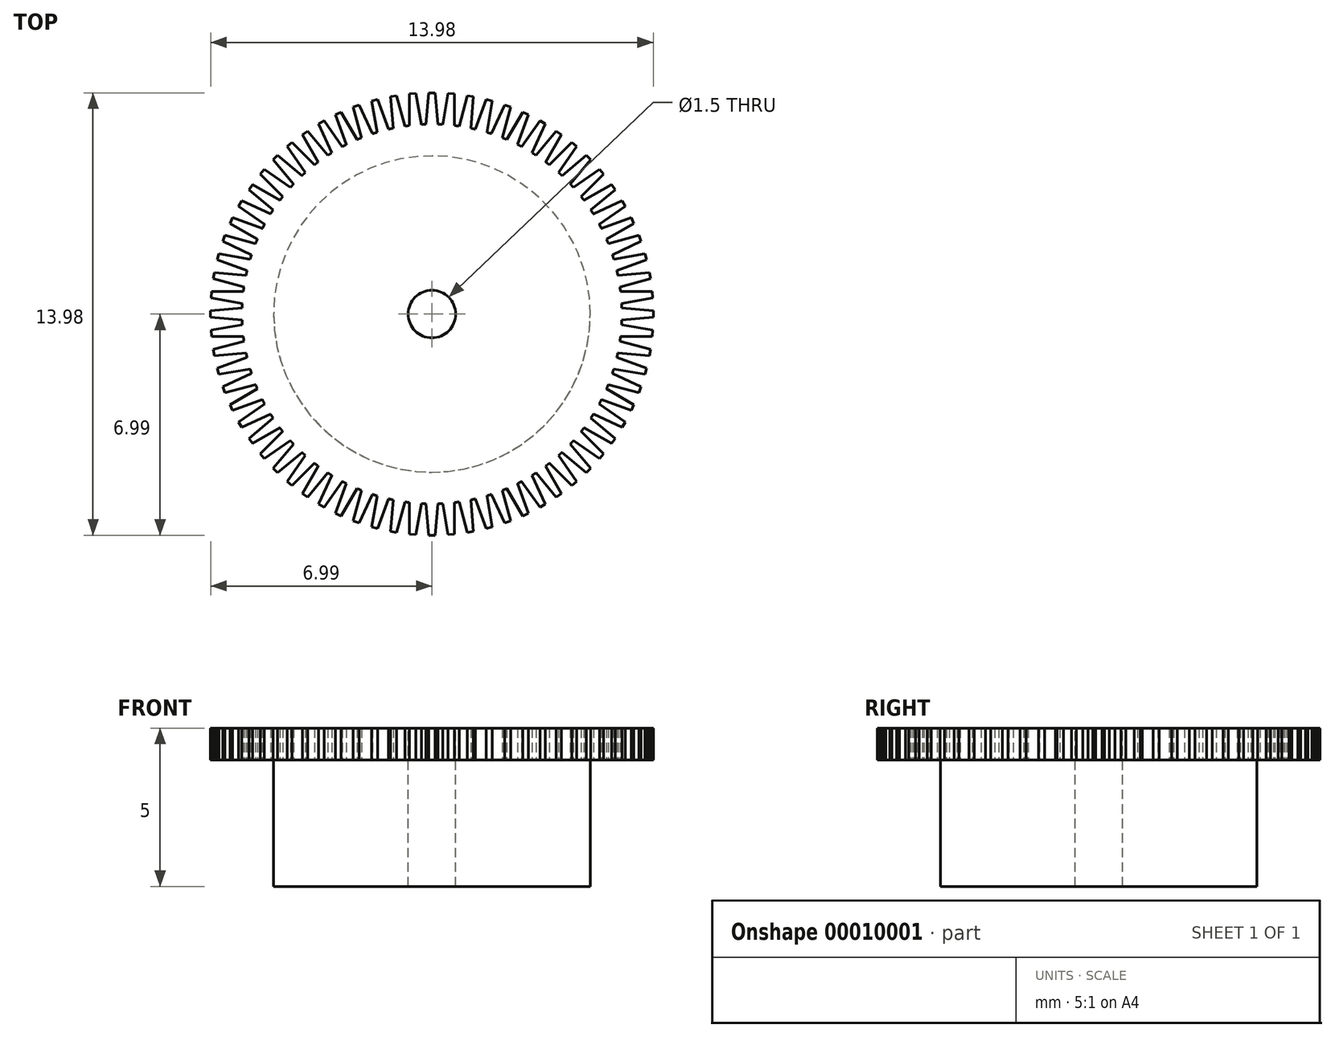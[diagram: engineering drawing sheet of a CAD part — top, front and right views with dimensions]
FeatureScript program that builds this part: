
annotation { "Feature Type Name" : "Feature", "Feature Type Description" : "" }
export const myFeature = defineFeature(function(context is Context, id is Id, definition is map)
    precondition{}
    {
        {
            var Q0;
            Q0=qCreatedBy(makeId("Top.planeOp"),FACE);
            var sketch = newSketch(context, id + "F0", { "sketchPlane" : qUnion([Q0])});
            skCircle(sketch, "E0", {"center": v(0, 0) * mm, "radius": 6 * mm});
            skLineSegment(sketch, "E1", {"start": v(0, 0) * mm, "end": v(0, 6) * mm, "construction": true});
            skLineSegment(sketch, "E2", {"start": v(-0.19, 6) * mm, "end": v(-0.1, 7) * mm});
            skLineSegment(sketch, "E3", {"start": v(-0.1, 7) * mm, "end": v(0, 7) * mm});
            skLineSegment(sketch, "E4.0.MirrorCS", {"start": v(0.1, 7) * mm, "end": v(0, 7) * mm});
            skLineSegment(sketch, "E5.0.MirrorCS", {"start": v(0.19, 6) * mm, "end": v(0.1, 7) * mm});
            skLineSegment(sketch, "E6.1.0", {"start": v(-0.7, 5.96) * mm, "end": v(-0.7, 6.96) * mm});
            skLineSegment(sketch, "E6.1.1", {"start": v(-0.7, 6.96) * mm, "end": v(-0.6, 6.97) * mm});
            skLineSegment(sketch, "E6.1.2", {"start": v(-0.5, 6.98) * mm, "end": v(-0.6, 6.97) * mm});
            skLineSegment(sketch, "E6.1.3", {"start": v(-0.34, 6) * mm, "end": v(-0.5, 6.98) * mm});
            skLineSegment(sketch, "E6.2.0", {"start": v(-1.23, 5.87) * mm, "end": v(-1.31, 6.87) * mm});
            skLineSegment(sketch, "E6.2.1", {"start": v(-1.31, 6.87) * mm, "end": v(-1.21, 6.89) * mm});
            skLineSegment(sketch, "E6.2.2", {"start": v(-1.12, 6.9) * mm, "end": v(-1.21, 6.89) * mm});
            skLineSegment(sketch, "E6.2.3", {"start": v(-0.86, 5.94) * mm, "end": v(-1.12, 6.9) * mm});
            skLineSegment(sketch, "E6.3.0", {"start": v(-1.73, 5.74) * mm, "end": v(-1.9, 6.73) * mm});
            skLineSegment(sketch, "E6.3.1", {"start": v(-1.9, 6.73) * mm, "end": v(-1.8, 6.75) * mm});
            skLineSegment(sketch, "E6.3.2", {"start": v(-1.71, 6.78) * mm, "end": v(-1.8, 6.75) * mm});
            skLineSegment(sketch, "E6.3.3", {"start": v(-1.37, 5.84) * mm, "end": v(-1.71, 6.78) * mm});
            skLineSegment(sketch, "E6.4.0", {"start": v(-2.23, 5.57) * mm, "end": v(-2.49, 6.54) * mm});
            skLineSegment(sketch, "E6.4.1", {"start": v(-2.49, 6.54) * mm, "end": v(-2.4, 6.57) * mm});
            skLineSegment(sketch, "E6.4.2", {"start": v(-2.3, 6.6) * mm, "end": v(-2.4, 6.57) * mm});
            skLineSegment(sketch, "E6.4.3", {"start": v(-1.88, 5.7) * mm, "end": v(-2.3, 6.6) * mm});
            skLineSegment(sketch, "E6.5.0", {"start": v(-2.7, 5.36) * mm, "end": v(-3.05, 6.3) * mm});
            skLineSegment(sketch, "E6.5.1", {"start": v(-3.05, 6.3) * mm, "end": v(-2.96, 6.34) * mm});
            skLineSegment(sketch, "E6.5.2", {"start": v(-2.86, 6.38) * mm, "end": v(-2.96, 6.34) * mm});
            skLineSegment(sketch, "E6.5.3", {"start": v(-2.36, 5.51) * mm, "end": v(-2.86, 6.38) * mm});
            skLineSegment(sketch, "E6.6.0", {"start": v(-3.16, 5.1) * mm, "end": v(-3.58, 6) * mm});
            skLineSegment(sketch, "E6.6.1", {"start": v(-3.58, 6) * mm, "end": v(-3.5, 6.06) * mm});
            skLineSegment(sketch, "E6.6.2", {"start": v(-3.41, 6.1) * mm, "end": v(-3.5, 6.06) * mm});
            skLineSegment(sketch, "E6.6.3", {"start": v(-2.84, 5.29) * mm, "end": v(-3.41, 6.1) * mm});
            skLineSegment(sketch, "E6.7.0", {"start": v(-3.6, 4.8) * mm, "end": v(-4.1, 5.67) * mm});
            skLineSegment(sketch, "E6.7.1", {"start": v(-4.1, 5.67) * mm, "end": v(-4.01, 5.73) * mm});
            skLineSegment(sketch, "E6.7.2", {"start": v(-3.93, 5.79) * mm, "end": v(-4.01, 5.73) * mm});
            skLineSegment(sketch, "E6.7.3", {"start": v(-3.29, 5.02) * mm, "end": v(-3.93, 5.79) * mm});
            skLineSegment(sketch, "E6.8.0", {"start": v(-4, 4.47) * mm, "end": v(-4.57, 5.3) * mm});
            skLineSegment(sketch, "E6.8.1", {"start": v(-4.57, 5.3) * mm, "end": v(-4.5, 5.36) * mm});
            skLineSegment(sketch, "E6.8.2", {"start": v(-4.42, 5.42) * mm, "end": v(-4.5, 5.36) * mm});
            skLineSegment(sketch, "E6.8.3", {"start": v(-3.71, 4.71) * mm, "end": v(-4.42, 5.42) * mm});
            skLineSegment(sketch, "E6.9.0", {"start": v(-4.37, 4.1) * mm, "end": v(-5.02, 4.87) * mm});
            skLineSegment(sketch, "E6.9.1", {"start": v(-5.02, 4.87) * mm, "end": v(-4.94, 4.94) * mm});
            skLineSegment(sketch, "E6.9.2", {"start": v(-4.87, 5.02) * mm, "end": v(-4.94, 4.94) * mm});
            skLineSegment(sketch, "E6.9.3", {"start": v(-4.1, 4.37) * mm, "end": v(-4.87, 5.02) * mm});
            skLineSegment(sketch, "E6.10.0", {"start": v(-4.71, 3.71) * mm, "end": v(-5.42, 4.42) * mm});
            skLineSegment(sketch, "E6.10.1", {"start": v(-5.42, 4.42) * mm, "end": v(-5.36, 4.5) * mm});
            skLineSegment(sketch, "E6.10.2", {"start": v(-5.3, 4.57) * mm, "end": v(-5.36, 4.5) * mm});
            skLineSegment(sketch, "E6.10.3", {"start": v(-4.47, 4) * mm, "end": v(-5.3, 4.57) * mm});
            skLineSegment(sketch, "E6.11.0", {"start": v(-5.02, 3.29) * mm, "end": v(-5.79, 3.93) * mm});
            skLineSegment(sketch, "E6.11.1", {"start": v(-5.79, 3.93) * mm, "end": v(-5.73, 4.01) * mm});
            skLineSegment(sketch, "E6.11.2", {"start": v(-5.67, 4.1) * mm, "end": v(-5.73, 4.01) * mm});
            skLineSegment(sketch, "E6.11.3", {"start": v(-4.8, 3.6) * mm, "end": v(-5.67, 4.1) * mm});
            skLineSegment(sketch, "E6.12.0", {"start": v(-5.29, 2.84) * mm, "end": v(-6.1, 3.41) * mm});
            skLineSegment(sketch, "E6.12.1", {"start": v(-6.1, 3.41) * mm, "end": v(-6.06, 3.5) * mm});
            skLineSegment(sketch, "E6.12.2", {"start": v(-6, 3.58) * mm, "end": v(-6.06, 3.5) * mm});
            skLineSegment(sketch, "E6.12.3", {"start": v(-5.1, 3.16) * mm, "end": v(-6, 3.58) * mm});
            skLineSegment(sketch, "E6.13.0", {"start": v(-5.51, 2.36) * mm, "end": v(-6.38, 2.86) * mm});
            skLineSegment(sketch, "E6.13.1", {"start": v(-6.38, 2.86) * mm, "end": v(-6.34, 2.96) * mm});
            skLineSegment(sketch, "E6.13.2", {"start": v(-6.3, 3.05) * mm, "end": v(-6.34, 2.96) * mm});
            skLineSegment(sketch, "E6.13.3", {"start": v(-5.36, 2.7) * mm, "end": v(-6.3, 3.05) * mm});
            skLineSegment(sketch, "E6.14.0", {"start": v(-5.7, 1.88) * mm, "end": v(-6.6, 2.3) * mm});
            skLineSegment(sketch, "E6.14.1", {"start": v(-6.6, 2.3) * mm, "end": v(-6.57, 2.4) * mm});
            skLineSegment(sketch, "E6.14.2", {"start": v(-6.54, 2.49) * mm, "end": v(-6.57, 2.4) * mm});
            skLineSegment(sketch, "E6.14.3", {"start": v(-5.57, 2.23) * mm, "end": v(-6.54, 2.49) * mm});
            skLineSegment(sketch, "E6.15.0", {"start": v(-5.84, 1.37) * mm, "end": v(-6.78, 1.71) * mm});
            skLineSegment(sketch, "E6.15.1", {"start": v(-6.78, 1.71) * mm, "end": v(-6.75, 1.8) * mm});
            skLineSegment(sketch, "E6.15.2", {"start": v(-6.73, 1.9) * mm, "end": v(-6.75, 1.8) * mm});
            skLineSegment(sketch, "E6.15.3", {"start": v(-5.74, 1.73) * mm, "end": v(-6.73, 1.9) * mm});
            skLineSegment(sketch, "E6.16.0", {"start": v(-5.94, 0.86) * mm, "end": v(-6.9, 1.12) * mm});
            skLineSegment(sketch, "E6.16.1", {"start": v(-6.9, 1.12) * mm, "end": v(-6.89, 1.21) * mm});
            skLineSegment(sketch, "E6.16.2", {"start": v(-6.87, 1.31) * mm, "end": v(-6.89, 1.21) * mm});
            skLineSegment(sketch, "E6.16.3", {"start": v(-5.87, 1.23) * mm, "end": v(-6.87, 1.31) * mm});
            skLineSegment(sketch, "E6.17.0", {"start": v(-6, 0.34) * mm, "end": v(-6.98, 0.5) * mm});
            skLineSegment(sketch, "E6.17.1", {"start": v(-6.98, 0.5) * mm, "end": v(-6.97, 0.6) * mm});
            skLineSegment(sketch, "E6.17.2", {"start": v(-6.96, 0.7) * mm, "end": v(-6.97, 0.6) * mm});
            skLineSegment(sketch, "E6.17.3", {"start": v(-5.96, 0.7) * mm, "end": v(-6.96, 0.7) * mm});
            skLineSegment(sketch, "E6.18.0", {"start": v(-6, -0.19) * mm, "end": v(-7, -0.1) * mm});
            skLineSegment(sketch, "E6.18.1", {"start": v(-7, -0.1) * mm, "end": v(-7, 0) * mm});
            skLineSegment(sketch, "E6.18.2", {"start": v(-7, 0.1) * mm, "end": v(-7, 0) * mm});
            skLineSegment(sketch, "E6.18.3", {"start": v(-6, 0.19) * mm, "end": v(-7, 0.1) * mm});
            skLineSegment(sketch, "E6.19.0", {"start": v(-5.96, -0.7) * mm, "end": v(-6.96, -0.7) * mm});
            skLineSegment(sketch, "E6.19.1", {"start": v(-6.96, -0.7) * mm, "end": v(-6.97, -0.6) * mm});
            skLineSegment(sketch, "E6.19.2", {"start": v(-6.98, -0.5) * mm, "end": v(-6.97, -0.6) * mm});
            skLineSegment(sketch, "E6.19.3", {"start": v(-6, -0.34) * mm, "end": v(-6.98, -0.5) * mm});
            skLineSegment(sketch, "E6.20.0", {"start": v(-5.87, -1.23) * mm, "end": v(-6.87, -1.31) * mm});
            skLineSegment(sketch, "E6.20.1", {"start": v(-6.87, -1.31) * mm, "end": v(-6.89, -1.21) * mm});
            skLineSegment(sketch, "E6.20.2", {"start": v(-6.9, -1.12) * mm, "end": v(-6.89, -1.21) * mm});
            skLineSegment(sketch, "E6.20.3", {"start": v(-5.94, -0.86) * mm, "end": v(-6.9, -1.12) * mm});
            skLineSegment(sketch, "E6.21.0", {"start": v(-5.74, -1.73) * mm, "end": v(-6.73, -1.9) * mm});
            skLineSegment(sketch, "E6.21.1", {"start": v(-6.73, -1.9) * mm, "end": v(-6.75, -1.8) * mm});
            skLineSegment(sketch, "E6.21.2", {"start": v(-6.78, -1.71) * mm, "end": v(-6.75, -1.8) * mm});
            skLineSegment(sketch, "E6.21.3", {"start": v(-5.84, -1.37) * mm, "end": v(-6.78, -1.71) * mm});
            skLineSegment(sketch, "E6.22.0", {"start": v(-5.57, -2.23) * mm, "end": v(-6.54, -2.49) * mm});
            skLineSegment(sketch, "E6.22.1", {"start": v(-6.54, -2.49) * mm, "end": v(-6.57, -2.4) * mm});
            skLineSegment(sketch, "E6.22.2", {"start": v(-6.6, -2.3) * mm, "end": v(-6.57, -2.4) * mm});
            skLineSegment(sketch, "E6.22.3", {"start": v(-5.7, -1.88) * mm, "end": v(-6.6, -2.3) * mm});
            skLineSegment(sketch, "E6.23.0", {"start": v(-5.36, -2.7) * mm, "end": v(-6.3, -3.05) * mm});
            skLineSegment(sketch, "E6.23.1", {"start": v(-6.3, -3.05) * mm, "end": v(-6.34, -2.96) * mm});
            skLineSegment(sketch, "E6.23.2", {"start": v(-6.38, -2.86) * mm, "end": v(-6.34, -2.96) * mm});
            skLineSegment(sketch, "E6.23.3", {"start": v(-5.51, -2.36) * mm, "end": v(-6.38, -2.86) * mm});
            skLineSegment(sketch, "E6.24.0", {"start": v(-5.1, -3.16) * mm, "end": v(-6, -3.58) * mm});
            skLineSegment(sketch, "E6.24.1", {"start": v(-6, -3.58) * mm, "end": v(-6.06, -3.5) * mm});
            skLineSegment(sketch, "E6.24.2", {"start": v(-6.1, -3.41) * mm, "end": v(-6.06, -3.5) * mm});
            skLineSegment(sketch, "E6.24.3", {"start": v(-5.29, -2.84) * mm, "end": v(-6.1, -3.41) * mm});
            skLineSegment(sketch, "E6.25.0", {"start": v(-4.8, -3.6) * mm, "end": v(-5.67, -4.1) * mm});
            skLineSegment(sketch, "E6.25.1", {"start": v(-5.67, -4.1) * mm, "end": v(-5.73, -4.01) * mm});
            skLineSegment(sketch, "E6.25.2", {"start": v(-5.79, -3.93) * mm, "end": v(-5.73, -4.01) * mm});
            skLineSegment(sketch, "E6.25.3", {"start": v(-5.02, -3.29) * mm, "end": v(-5.79, -3.93) * mm});
            skLineSegment(sketch, "E6.26.0", {"start": v(-4.47, -4) * mm, "end": v(-5.3, -4.57) * mm});
            skLineSegment(sketch, "E6.26.1", {"start": v(-5.3, -4.57) * mm, "end": v(-5.36, -4.5) * mm});
            skLineSegment(sketch, "E6.26.2", {"start": v(-5.42, -4.42) * mm, "end": v(-5.36, -4.5) * mm});
            skLineSegment(sketch, "E6.26.3", {"start": v(-4.71, -3.71) * mm, "end": v(-5.42, -4.42) * mm});
            skLineSegment(sketch, "E6.27.0", {"start": v(-4.1, -4.37) * mm, "end": v(-4.87, -5.02) * mm});
            skLineSegment(sketch, "E6.27.1", {"start": v(-4.87, -5.02) * mm, "end": v(-4.94, -4.94) * mm});
            skLineSegment(sketch, "E6.27.2", {"start": v(-5.02, -4.87) * mm, "end": v(-4.94, -4.94) * mm});
            skLineSegment(sketch, "E6.27.3", {"start": v(-4.37, -4.1) * mm, "end": v(-5.02, -4.87) * mm});
            skLineSegment(sketch, "E6.28.0", {"start": v(-3.71, -4.71) * mm, "end": v(-4.42, -5.42) * mm});
            skLineSegment(sketch, "E6.28.1", {"start": v(-4.42, -5.42) * mm, "end": v(-4.5, -5.36) * mm});
            skLineSegment(sketch, "E6.28.2", {"start": v(-4.57, -5.3) * mm, "end": v(-4.5, -5.36) * mm});
            skLineSegment(sketch, "E6.28.3", {"start": v(-4, -4.47) * mm, "end": v(-4.57, -5.3) * mm});
            skLineSegment(sketch, "E6.29.0", {"start": v(-3.29, -5.02) * mm, "end": v(-3.93, -5.79) * mm});
            skLineSegment(sketch, "E6.29.1", {"start": v(-3.93, -5.79) * mm, "end": v(-4.01, -5.73) * mm});
            skLineSegment(sketch, "E6.29.2", {"start": v(-4.1, -5.67) * mm, "end": v(-4.01, -5.73) * mm});
            skLineSegment(sketch, "E6.29.3", {"start": v(-3.6, -4.8) * mm, "end": v(-4.1, -5.67) * mm});
            skLineSegment(sketch, "E6.30.0", {"start": v(-2.84, -5.29) * mm, "end": v(-3.41, -6.1) * mm});
            skLineSegment(sketch, "E6.30.1", {"start": v(-3.41, -6.1) * mm, "end": v(-3.5, -6.06) * mm});
            skLineSegment(sketch, "E6.30.2", {"start": v(-3.58, -6) * mm, "end": v(-3.5, -6.06) * mm});
            skLineSegment(sketch, "E6.30.3", {"start": v(-3.16, -5.1) * mm, "end": v(-3.58, -6) * mm});
            skLineSegment(sketch, "E6.31.0", {"start": v(-2.36, -5.51) * mm, "end": v(-2.86, -6.38) * mm});
            skLineSegment(sketch, "E6.31.1", {"start": v(-2.86, -6.38) * mm, "end": v(-2.96, -6.34) * mm});
            skLineSegment(sketch, "E6.31.2", {"start": v(-3.05, -6.3) * mm, "end": v(-2.96, -6.34) * mm});
            skLineSegment(sketch, "E6.31.3", {"start": v(-2.7, -5.36) * mm, "end": v(-3.05, -6.3) * mm});
            skLineSegment(sketch, "E6.32.0", {"start": v(-1.88, -5.7) * mm, "end": v(-2.3, -6.6) * mm});
            skLineSegment(sketch, "E6.32.1", {"start": v(-2.3, -6.6) * mm, "end": v(-2.4, -6.57) * mm});
            skLineSegment(sketch, "E6.32.2", {"start": v(-2.49, -6.54) * mm, "end": v(-2.4, -6.57) * mm});
            skLineSegment(sketch, "E6.32.3", {"start": v(-2.23, -5.57) * mm, "end": v(-2.49, -6.54) * mm});
            skLineSegment(sketch, "E6.33.0", {"start": v(-1.37, -5.84) * mm, "end": v(-1.71, -6.78) * mm});
            skLineSegment(sketch, "E6.33.1", {"start": v(-1.71, -6.78) * mm, "end": v(-1.8, -6.75) * mm});
            skLineSegment(sketch, "E6.33.2", {"start": v(-1.9, -6.73) * mm, "end": v(-1.8, -6.75) * mm});
            skLineSegment(sketch, "E6.33.3", {"start": v(-1.73, -5.74) * mm, "end": v(-1.9, -6.73) * mm});
            skLineSegment(sketch, "E6.34.0", {"start": v(-0.86, -5.94) * mm, "end": v(-1.12, -6.9) * mm});
            skLineSegment(sketch, "E6.34.1", {"start": v(-1.12, -6.9) * mm, "end": v(-1.21, -6.89) * mm});
            skLineSegment(sketch, "E6.34.2", {"start": v(-1.31, -6.87) * mm, "end": v(-1.21, -6.89) * mm});
            skLineSegment(sketch, "E6.34.3", {"start": v(-1.23, -5.87) * mm, "end": v(-1.31, -6.87) * mm});
            skLineSegment(sketch, "E6.35.0", {"start": v(-0.34, -6) * mm, "end": v(-0.5, -6.98) * mm});
            skLineSegment(sketch, "E6.35.1", {"start": v(-0.5, -6.98) * mm, "end": v(-0.6, -6.97) * mm});
            skLineSegment(sketch, "E6.35.2", {"start": v(-0.7, -6.96) * mm, "end": v(-0.6, -6.97) * mm});
            skLineSegment(sketch, "E6.35.3", {"start": v(-0.7, -5.96) * mm, "end": v(-0.7, -6.96) * mm});
            skLineSegment(sketch, "E6.36.0", {"start": v(0.19, -6) * mm, "end": v(0.1, -7) * mm});
            skLineSegment(sketch, "E6.36.1", {"start": v(0.1, -7) * mm, "end": v(0, -7) * mm});
            skLineSegment(sketch, "E6.36.2", {"start": v(-0.1, -7) * mm, "end": v(0, -7) * mm});
            skLineSegment(sketch, "E6.36.3", {"start": v(-0.19, -6) * mm, "end": v(-0.1, -7) * mm});
            skLineSegment(sketch, "E6.37.0", {"start": v(0.7, -5.96) * mm, "end": v(0.7, -6.96) * mm});
            skLineSegment(sketch, "E6.37.1", {"start": v(0.7, -6.96) * mm, "end": v(0.6, -6.97) * mm});
            skLineSegment(sketch, "E6.37.2", {"start": v(0.5, -6.98) * mm, "end": v(0.6, -6.97) * mm});
            skLineSegment(sketch, "E6.37.3", {"start": v(0.34, -6) * mm, "end": v(0.5, -6.98) * mm});
            skLineSegment(sketch, "E6.38.0", {"start": v(1.23, -5.87) * mm, "end": v(1.31, -6.87) * mm});
            skLineSegment(sketch, "E6.38.1", {"start": v(1.31, -6.87) * mm, "end": v(1.21, -6.89) * mm});
            skLineSegment(sketch, "E6.38.2", {"start": v(1.12, -6.9) * mm, "end": v(1.21, -6.89) * mm});
            skLineSegment(sketch, "E6.38.3", {"start": v(0.86, -5.94) * mm, "end": v(1.12, -6.9) * mm});
            skLineSegment(sketch, "E6.39.0", {"start": v(1.73, -5.74) * mm, "end": v(1.9, -6.73) * mm});
            skLineSegment(sketch, "E6.39.1", {"start": v(1.9, -6.73) * mm, "end": v(1.8, -6.75) * mm});
            skLineSegment(sketch, "E6.39.2", {"start": v(1.71, -6.78) * mm, "end": v(1.8, -6.75) * mm});
            skLineSegment(sketch, "E6.39.3", {"start": v(1.37, -5.84) * mm, "end": v(1.71, -6.78) * mm});
            skLineSegment(sketch, "E6.40.0", {"start": v(2.23, -5.57) * mm, "end": v(2.49, -6.54) * mm});
            skLineSegment(sketch, "E6.40.1", {"start": v(2.49, -6.54) * mm, "end": v(2.4, -6.57) * mm});
            skLineSegment(sketch, "E6.40.2", {"start": v(2.3, -6.6) * mm, "end": v(2.4, -6.57) * mm});
            skLineSegment(sketch, "E6.40.3", {"start": v(1.88, -5.7) * mm, "end": v(2.3, -6.6) * mm});
            skLineSegment(sketch, "E6.41.0", {"start": v(2.7, -5.36) * mm, "end": v(3.05, -6.3) * mm});
            skLineSegment(sketch, "E6.41.1", {"start": v(3.05, -6.3) * mm, "end": v(2.96, -6.34) * mm});
            skLineSegment(sketch, "E6.41.2", {"start": v(2.86, -6.38) * mm, "end": v(2.96, -6.34) * mm});
            skLineSegment(sketch, "E6.41.3", {"start": v(2.36, -5.51) * mm, "end": v(2.86, -6.38) * mm});
            skLineSegment(sketch, "E6.42.0", {"start": v(3.16, -5.1) * mm, "end": v(3.58, -6) * mm});
            skLineSegment(sketch, "E6.42.1", {"start": v(3.58, -6) * mm, "end": v(3.5, -6.06) * mm});
            skLineSegment(sketch, "E6.42.2", {"start": v(3.41, -6.1) * mm, "end": v(3.5, -6.06) * mm});
            skLineSegment(sketch, "E6.42.3", {"start": v(2.84, -5.29) * mm, "end": v(3.41, -6.1) * mm});
            skLineSegment(sketch, "E6.43.0", {"start": v(3.6, -4.8) * mm, "end": v(4.1, -5.67) * mm});
            skLineSegment(sketch, "E6.43.1", {"start": v(4.1, -5.67) * mm, "end": v(4.01, -5.73) * mm});
            skLineSegment(sketch, "E6.43.2", {"start": v(3.93, -5.79) * mm, "end": v(4.01, -5.73) * mm});
            skLineSegment(sketch, "E6.43.3", {"start": v(3.29, -5.02) * mm, "end": v(3.93, -5.79) * mm});
            skLineSegment(sketch, "E6.44.0", {"start": v(4, -4.47) * mm, "end": v(4.57, -5.3) * mm});
            skLineSegment(sketch, "E6.44.1", {"start": v(4.57, -5.3) * mm, "end": v(4.5, -5.36) * mm});
            skLineSegment(sketch, "E6.44.2", {"start": v(4.42, -5.42) * mm, "end": v(4.5, -5.36) * mm});
            skLineSegment(sketch, "E6.44.3", {"start": v(3.71, -4.71) * mm, "end": v(4.42, -5.42) * mm});
            skLineSegment(sketch, "E6.45.0", {"start": v(4.37, -4.1) * mm, "end": v(5.02, -4.87) * mm});
            skLineSegment(sketch, "E6.45.1", {"start": v(5.02, -4.87) * mm, "end": v(4.94, -4.94) * mm});
            skLineSegment(sketch, "E6.45.2", {"start": v(4.87, -5.02) * mm, "end": v(4.94, -4.94) * mm});
            skLineSegment(sketch, "E6.45.3", {"start": v(4.1, -4.37) * mm, "end": v(4.87, -5.02) * mm});
            skLineSegment(sketch, "E6.46.0", {"start": v(4.71, -3.71) * mm, "end": v(5.42, -4.42) * mm});
            skLineSegment(sketch, "E6.46.1", {"start": v(5.42, -4.42) * mm, "end": v(5.36, -4.5) * mm});
            skLineSegment(sketch, "E6.46.2", {"start": v(5.3, -4.57) * mm, "end": v(5.36, -4.5) * mm});
            skLineSegment(sketch, "E6.46.3", {"start": v(4.47, -4) * mm, "end": v(5.3, -4.57) * mm});
            skLineSegment(sketch, "E6.47.0", {"start": v(5.02, -3.29) * mm, "end": v(5.79, -3.93) * mm});
            skLineSegment(sketch, "E6.47.1", {"start": v(5.79, -3.93) * mm, "end": v(5.73, -4.01) * mm});
            skLineSegment(sketch, "E6.47.2", {"start": v(5.67, -4.1) * mm, "end": v(5.73, -4.01) * mm});
            skLineSegment(sketch, "E6.47.3", {"start": v(4.8, -3.6) * mm, "end": v(5.67, -4.1) * mm});
            skLineSegment(sketch, "E6.48.0", {"start": v(5.29, -2.84) * mm, "end": v(6.1, -3.41) * mm});
            skLineSegment(sketch, "E6.48.1", {"start": v(6.1, -3.41) * mm, "end": v(6.06, -3.5) * mm});
            skLineSegment(sketch, "E6.48.2", {"start": v(6, -3.58) * mm, "end": v(6.06, -3.5) * mm});
            skLineSegment(sketch, "E6.48.3", {"start": v(5.1, -3.16) * mm, "end": v(6, -3.58) * mm});
            skLineSegment(sketch, "E6.49.0", {"start": v(5.51, -2.36) * mm, "end": v(6.38, -2.86) * mm});
            skLineSegment(sketch, "E6.49.1", {"start": v(6.38, -2.86) * mm, "end": v(6.34, -2.96) * mm});
            skLineSegment(sketch, "E6.49.2", {"start": v(6.3, -3.05) * mm, "end": v(6.34, -2.96) * mm});
            skLineSegment(sketch, "E6.49.3", {"start": v(5.36, -2.7) * mm, "end": v(6.3, -3.05) * mm});
            skLineSegment(sketch, "E6.50.0", {"start": v(5.7, -1.88) * mm, "end": v(6.6, -2.3) * mm});
            skLineSegment(sketch, "E6.50.1", {"start": v(6.6, -2.3) * mm, "end": v(6.57, -2.4) * mm});
            skLineSegment(sketch, "E6.50.2", {"start": v(6.54, -2.49) * mm, "end": v(6.57, -2.4) * mm});
            skLineSegment(sketch, "E6.50.3", {"start": v(5.57, -2.23) * mm, "end": v(6.54, -2.49) * mm});
            skLineSegment(sketch, "E6.51.0", {"start": v(5.84, -1.37) * mm, "end": v(6.78, -1.71) * mm});
            skLineSegment(sketch, "E6.51.1", {"start": v(6.78, -1.71) * mm, "end": v(6.75, -1.8) * mm});
            skLineSegment(sketch, "E6.51.2", {"start": v(6.73, -1.9) * mm, "end": v(6.75, -1.8) * mm});
            skLineSegment(sketch, "E6.51.3", {"start": v(5.74, -1.73) * mm, "end": v(6.73, -1.9) * mm});
            skLineSegment(sketch, "E6.52.0", {"start": v(5.94, -0.86) * mm, "end": v(6.9, -1.12) * mm});
            skLineSegment(sketch, "E6.52.1", {"start": v(6.9, -1.12) * mm, "end": v(6.89, -1.21) * mm});
            skLineSegment(sketch, "E6.52.2", {"start": v(6.87, -1.31) * mm, "end": v(6.89, -1.21) * mm});
            skLineSegment(sketch, "E6.52.3", {"start": v(5.87, -1.23) * mm, "end": v(6.87, -1.31) * mm});
            skLineSegment(sketch, "E6.53.0", {"start": v(6, -0.34) * mm, "end": v(6.98, -0.5) * mm});
            skLineSegment(sketch, "E6.53.1", {"start": v(6.98, -0.5) * mm, "end": v(6.97, -0.6) * mm});
            skLineSegment(sketch, "E6.53.2", {"start": v(6.96, -0.7) * mm, "end": v(6.97, -0.6) * mm});
            skLineSegment(sketch, "E6.53.3", {"start": v(5.96, -0.7) * mm, "end": v(6.96, -0.7) * mm});
            skLineSegment(sketch, "E6.54.0", {"start": v(6, 0.19) * mm, "end": v(7, 0.1) * mm});
            skLineSegment(sketch, "E6.54.1", {"start": v(7, 0.1) * mm, "end": v(7, 0) * mm});
            skLineSegment(sketch, "E6.54.2", {"start": v(7, -0.1) * mm, "end": v(7, 0) * mm});
            skLineSegment(sketch, "E6.54.3", {"start": v(6, -0.19) * mm, "end": v(7, -0.1) * mm});
            skLineSegment(sketch, "E6.55.0", {"start": v(5.96, 0.7) * mm, "end": v(6.96, 0.7) * mm});
            skLineSegment(sketch, "E6.55.1", {"start": v(6.96, 0.7) * mm, "end": v(6.97, 0.6) * mm});
            skLineSegment(sketch, "E6.55.2", {"start": v(6.98, 0.5) * mm, "end": v(6.97, 0.6) * mm});
            skLineSegment(sketch, "E6.55.3", {"start": v(6, 0.34) * mm, "end": v(6.98, 0.5) * mm});
            skLineSegment(sketch, "E6.56.0", {"start": v(5.87, 1.23) * mm, "end": v(6.87, 1.31) * mm});
            skLineSegment(sketch, "E6.56.1", {"start": v(6.87, 1.31) * mm, "end": v(6.89, 1.21) * mm});
            skLineSegment(sketch, "E6.56.2", {"start": v(6.9, 1.12) * mm, "end": v(6.89, 1.21) * mm});
            skLineSegment(sketch, "E6.56.3", {"start": v(5.94, 0.86) * mm, "end": v(6.9, 1.12) * mm});
            skLineSegment(sketch, "E6.57.0", {"start": v(5.74, 1.73) * mm, "end": v(6.73, 1.9) * mm});
            skLineSegment(sketch, "E6.57.1", {"start": v(6.73, 1.9) * mm, "end": v(6.75, 1.8) * mm});
            skLineSegment(sketch, "E6.57.2", {"start": v(6.78, 1.71) * mm, "end": v(6.75, 1.8) * mm});
            skLineSegment(sketch, "E6.57.3", {"start": v(5.84, 1.37) * mm, "end": v(6.78, 1.71) * mm});
            skLineSegment(sketch, "E6.58.0", {"start": v(5.57, 2.23) * mm, "end": v(6.54, 2.49) * mm});
            skLineSegment(sketch, "E6.58.1", {"start": v(6.54, 2.49) * mm, "end": v(6.57, 2.4) * mm});
            skLineSegment(sketch, "E6.58.2", {"start": v(6.6, 2.3) * mm, "end": v(6.57, 2.4) * mm});
            skLineSegment(sketch, "E6.58.3", {"start": v(5.7, 1.88) * mm, "end": v(6.6, 2.3) * mm});
            skLineSegment(sketch, "E6.59.0", {"start": v(5.36, 2.7) * mm, "end": v(6.3, 3.05) * mm});
            skLineSegment(sketch, "E6.59.1", {"start": v(6.3, 3.05) * mm, "end": v(6.34, 2.96) * mm});
            skLineSegment(sketch, "E6.59.2", {"start": v(6.38, 2.86) * mm, "end": v(6.34, 2.96) * mm});
            skLineSegment(sketch, "E6.59.3", {"start": v(5.51, 2.36) * mm, "end": v(6.38, 2.86) * mm});
            skLineSegment(sketch, "E6.60.0", {"start": v(5.1, 3.16) * mm, "end": v(6, 3.58) * mm});
            skLineSegment(sketch, "E6.60.1", {"start": v(6, 3.58) * mm, "end": v(6.06, 3.5) * mm});
            skLineSegment(sketch, "E6.60.2", {"start": v(6.1, 3.41) * mm, "end": v(6.06, 3.5) * mm});
            skLineSegment(sketch, "E6.60.3", {"start": v(5.29, 2.84) * mm, "end": v(6.1, 3.41) * mm});
            skLineSegment(sketch, "E6.61.0", {"start": v(4.8, 3.6) * mm, "end": v(5.67, 4.1) * mm});
            skLineSegment(sketch, "E6.61.1", {"start": v(5.67, 4.1) * mm, "end": v(5.73, 4.01) * mm});
            skLineSegment(sketch, "E6.61.2", {"start": v(5.79, 3.93) * mm, "end": v(5.73, 4.01) * mm});
            skLineSegment(sketch, "E6.61.3", {"start": v(5.02, 3.29) * mm, "end": v(5.79, 3.93) * mm});
            skLineSegment(sketch, "E6.62.0", {"start": v(4.47, 4) * mm, "end": v(5.3, 4.57) * mm});
            skLineSegment(sketch, "E6.62.1", {"start": v(5.3, 4.57) * mm, "end": v(5.36, 4.5) * mm});
            skLineSegment(sketch, "E6.62.2", {"start": v(5.42, 4.42) * mm, "end": v(5.36, 4.5) * mm});
            skLineSegment(sketch, "E6.62.3", {"start": v(4.71, 3.71) * mm, "end": v(5.42, 4.42) * mm});
            skLineSegment(sketch, "E6.63.0", {"start": v(4.1, 4.37) * mm, "end": v(4.87, 5.02) * mm});
            skLineSegment(sketch, "E6.63.1", {"start": v(4.87, 5.02) * mm, "end": v(4.94, 4.94) * mm});
            skLineSegment(sketch, "E6.63.2", {"start": v(5.02, 4.87) * mm, "end": v(4.94, 4.94) * mm});
            skLineSegment(sketch, "E6.63.3", {"start": v(4.37, 4.1) * mm, "end": v(5.02, 4.87) * mm});
            skLineSegment(sketch, "E6.64.0", {"start": v(3.71, 4.71) * mm, "end": v(4.42, 5.42) * mm});
            skLineSegment(sketch, "E6.64.1", {"start": v(4.42, 5.42) * mm, "end": v(4.5, 5.36) * mm});
            skLineSegment(sketch, "E6.64.2", {"start": v(4.57, 5.3) * mm, "end": v(4.5, 5.36) * mm});
            skLineSegment(sketch, "E6.64.3", {"start": v(4, 4.47) * mm, "end": v(4.57, 5.3) * mm});
            skLineSegment(sketch, "E6.65.0", {"start": v(3.29, 5.02) * mm, "end": v(3.93, 5.79) * mm});
            skLineSegment(sketch, "E6.65.1", {"start": v(3.93, 5.79) * mm, "end": v(4.01, 5.73) * mm});
            skLineSegment(sketch, "E6.65.2", {"start": v(4.1, 5.67) * mm, "end": v(4.01, 5.73) * mm});
            skLineSegment(sketch, "E6.65.3", {"start": v(3.6, 4.8) * mm, "end": v(4.1, 5.67) * mm});
            skLineSegment(sketch, "E6.66.0", {"start": v(2.84, 5.29) * mm, "end": v(3.41, 6.1) * mm});
            skLineSegment(sketch, "E6.66.1", {"start": v(3.41, 6.1) * mm, "end": v(3.5, 6.06) * mm});
            skLineSegment(sketch, "E6.66.2", {"start": v(3.58, 6) * mm, "end": v(3.5, 6.06) * mm});
            skLineSegment(sketch, "E6.66.3", {"start": v(3.16, 5.1) * mm, "end": v(3.58, 6) * mm});
            skLineSegment(sketch, "E6.67.0", {"start": v(2.36, 5.51) * mm, "end": v(2.86, 6.38) * mm});
            skLineSegment(sketch, "E6.67.1", {"start": v(2.86, 6.38) * mm, "end": v(2.96, 6.34) * mm});
            skLineSegment(sketch, "E6.67.2", {"start": v(3.05, 6.3) * mm, "end": v(2.96, 6.34) * mm});
            skLineSegment(sketch, "E6.67.3", {"start": v(2.7, 5.36) * mm, "end": v(3.05, 6.3) * mm});
            skLineSegment(sketch, "E6.68.0", {"start": v(1.88, 5.7) * mm, "end": v(2.3, 6.6) * mm});
            skLineSegment(sketch, "E6.68.1", {"start": v(2.3, 6.6) * mm, "end": v(2.4, 6.57) * mm});
            skLineSegment(sketch, "E6.68.2", {"start": v(2.49, 6.54) * mm, "end": v(2.4, 6.57) * mm});
            skLineSegment(sketch, "E6.68.3", {"start": v(2.23, 5.57) * mm, "end": v(2.49, 6.54) * mm});
            skLineSegment(sketch, "E6.69.0", {"start": v(1.37, 5.84) * mm, "end": v(1.71, 6.78) * mm});
            skLineSegment(sketch, "E6.69.1", {"start": v(1.71, 6.78) * mm, "end": v(1.8, 6.75) * mm});
            skLineSegment(sketch, "E6.69.2", {"start": v(1.9, 6.73) * mm, "end": v(1.8, 6.75) * mm});
            skLineSegment(sketch, "E6.69.3", {"start": v(1.73, 5.74) * mm, "end": v(1.9, 6.73) * mm});
            skLineSegment(sketch, "E6.70.0", {"start": v(0.86, 5.94) * mm, "end": v(1.12, 6.9) * mm});
            skLineSegment(sketch, "E6.70.1", {"start": v(1.12, 6.9) * mm, "end": v(1.21, 6.89) * mm});
            skLineSegment(sketch, "E6.70.2", {"start": v(1.31, 6.87) * mm, "end": v(1.21, 6.89) * mm});
            skLineSegment(sketch, "E6.70.3", {"start": v(1.23, 5.87) * mm, "end": v(1.31, 6.87) * mm});
            skLineSegment(sketch, "E6.71.0", {"start": v(0.34, 6) * mm, "end": v(0.5, 6.98) * mm});
            skLineSegment(sketch, "E6.71.1", {"start": v(0.5, 6.98) * mm, "end": v(0.6, 6.97) * mm});
            skLineSegment(sketch, "E6.71.2", {"start": v(0.7, 6.96) * mm, "end": v(0.6, 6.97) * mm});
            skLineSegment(sketch, "E6.71.3", {"start": v(0.7, 5.96) * mm, "end": v(0.7, 6.96) * mm});
            skSolve(sketch);
        }
        {
            var Q0;
            Q0=qSketchRegion(id+"F0",true);
            extrude(context, id + "F1", {"entities" : qUnion([Q0]), "depth" : 1 * mm});
        }
        {
            var Q0;
            Q0=makeQuery(id+"F1.opExtrude","CAP_FACE",FACE,{"disambiguationData":[OSD([sQuery(id+"F0.wireOp",EDGE,"E0"),sQuery(id+"F0.wireOp",EDGE,"E2"),sQuery(id+"F0.wireOp",EDGE,"E3"),sQuery(id+"F0.wireOp",EDGE,"E4.0.MirrorCS"),sQuery(id+"F0.wireOp",EDGE,"E5.0.MirrorCS"),sQuery(id+"F0.wireOp",EDGE,"E6.1.0"),sQuery(id+"F0.wireOp",EDGE,"E6.1.1"),sQuery(id+"F0.wireOp",EDGE,"E6.1.2"),sQuery(id+"F0.wireOp",EDGE,"E6.1.3"),sQuery(id+"F0.wireOp",EDGE,"E6.2.0"),sQuery(id+"F0.wireOp",EDGE,"E6.2.1"),sQuery(id+"F0.wireOp",EDGE,"E6.2.2"),sQuery(id+"F0.wireOp",EDGE,"E6.2.3"),sQuery(id+"F0.wireOp",EDGE,"E6.3.0"),sQuery(id+"F0.wireOp",EDGE,"E6.3.1"),sQuery(id+"F0.wireOp",EDGE,"E6.3.2"),sQuery(id+"F0.wireOp",EDGE,"E6.3.3"),sQuery(id+"F0.wireOp",EDGE,"E6.4.0"),sQuery(id+"F0.wireOp",EDGE,"E6.4.1"),sQuery(id+"F0.wireOp",EDGE,"E6.4.2"),sQuery(id+"F0.wireOp",EDGE,"E6.4.3"),sQuery(id+"F0.wireOp",EDGE,"E6.5.0"),sQuery(id+"F0.wireOp",EDGE,"E6.5.1"),sQuery(id+"F0.wireOp",EDGE,"E6.5.2"),sQuery(id+"F0.wireOp",EDGE,"E6.5.3"),sQuery(id+"F0.wireOp",EDGE,"E6.6.0"),sQuery(id+"F0.wireOp",EDGE,"E6.6.1"),sQuery(id+"F0.wireOp",EDGE,"E6.6.2"),sQuery(id+"F0.wireOp",EDGE,"E6.6.3"),sQuery(id+"F0.wireOp",EDGE,"E6.7.0"),sQuery(id+"F0.wireOp",EDGE,"E6.7.1"),sQuery(id+"F0.wireOp",EDGE,"E6.7.2"),sQuery(id+"F0.wireOp",EDGE,"E6.7.3"),sQuery(id+"F0.wireOp",EDGE,"E6.8.0"),sQuery(id+"F0.wireOp",EDGE,"E6.8.1"),sQuery(id+"F0.wireOp",EDGE,"E6.8.2"),sQuery(id+"F0.wireOp",EDGE,"E6.8.3"),sQuery(id+"F0.wireOp",EDGE,"E6.9.0"),sQuery(id+"F0.wireOp",EDGE,"E6.9.1"),sQuery(id+"F0.wireOp",EDGE,"E6.9.2"),sQuery(id+"F0.wireOp",EDGE,"E6.9.3"),sQuery(id+"F0.wireOp",EDGE,"E6.10.0"),sQuery(id+"F0.wireOp",EDGE,"E6.10.1"),sQuery(id+"F0.wireOp",EDGE,"E6.10.2"),sQuery(id+"F0.wireOp",EDGE,"E6.10.3"),sQuery(id+"F0.wireOp",EDGE,"E6.11.0"),sQuery(id+"F0.wireOp",EDGE,"E6.11.1"),sQuery(id+"F0.wireOp",EDGE,"E6.11.2"),sQuery(id+"F0.wireOp",EDGE,"E6.11.3"),sQuery(id+"F0.wireOp",EDGE,"E6.12.0"),sQuery(id+"F0.wireOp",EDGE,"E6.12.1"),sQuery(id+"F0.wireOp",EDGE,"E6.12.2"),sQuery(id+"F0.wireOp",EDGE,"E6.12.3"),sQuery(id+"F0.wireOp",EDGE,"E6.13.0"),sQuery(id+"F0.wireOp",EDGE,"E6.13.1"),sQuery(id+"F0.wireOp",EDGE,"E6.13.2"),sQuery(id+"F0.wireOp",EDGE,"E6.13.3"),sQuery(id+"F0.wireOp",EDGE,"E6.14.0"),sQuery(id+"F0.wireOp",EDGE,"E6.14.1"),sQuery(id+"F0.wireOp",EDGE,"E6.14.2"),sQuery(id+"F0.wireOp",EDGE,"E6.14.3"),sQuery(id+"F0.wireOp",EDGE,"E6.15.0"),sQuery(id+"F0.wireOp",EDGE,"E6.15.1"),sQuery(id+"F0.wireOp",EDGE,"E6.15.2"),sQuery(id+"F0.wireOp",EDGE,"E6.15.3"),sQuery(id+"F0.wireOp",EDGE,"E6.16.0"),sQuery(id+"F0.wireOp",EDGE,"E6.16.1"),sQuery(id+"F0.wireOp",EDGE,"E6.16.2"),sQuery(id+"F0.wireOp",EDGE,"E6.16.3"),sQuery(id+"F0.wireOp",EDGE,"E6.17.0"),sQuery(id+"F0.wireOp",EDGE,"E6.17.1"),sQuery(id+"F0.wireOp",EDGE,"E6.17.2"),sQuery(id+"F0.wireOp",EDGE,"E6.17.3"),sQuery(id+"F0.wireOp",EDGE,"E6.18.0"),sQuery(id+"F0.wireOp",EDGE,"E6.18.1"),sQuery(id+"F0.wireOp",EDGE,"E6.18.2"),sQuery(id+"F0.wireOp",EDGE,"E6.18.3"),sQuery(id+"F0.wireOp",EDGE,"E6.19.0"),sQuery(id+"F0.wireOp",EDGE,"E6.19.1"),sQuery(id+"F0.wireOp",EDGE,"E6.19.2"),sQuery(id+"F0.wireOp",EDGE,"E6.19.3"),sQuery(id+"F0.wireOp",EDGE,"E6.20.0"),sQuery(id+"F0.wireOp",EDGE,"E6.20.1"),sQuery(id+"F0.wireOp",EDGE,"E6.20.2"),sQuery(id+"F0.wireOp",EDGE,"E6.20.3"),sQuery(id+"F0.wireOp",EDGE,"E6.21.0"),sQuery(id+"F0.wireOp",EDGE,"E6.21.1"),sQuery(id+"F0.wireOp",EDGE,"E6.21.2"),sQuery(id+"F0.wireOp",EDGE,"E6.21.3"),sQuery(id+"F0.wireOp",EDGE,"E6.22.0"),sQuery(id+"F0.wireOp",EDGE,"E6.22.1"),sQuery(id+"F0.wireOp",EDGE,"E6.22.2"),sQuery(id+"F0.wireOp",EDGE,"E6.22.3"),sQuery(id+"F0.wireOp",EDGE,"E6.23.0"),sQuery(id+"F0.wireOp",EDGE,"E6.23.1"),sQuery(id+"F0.wireOp",EDGE,"E6.23.2"),sQuery(id+"F0.wireOp",EDGE,"E6.23.3"),sQuery(id+"F0.wireOp",EDGE,"E6.24.0"),sQuery(id+"F0.wireOp",EDGE,"E6.24.1"),sQuery(id+"F0.wireOp",EDGE,"E6.24.2"),sQuery(id+"F0.wireOp",EDGE,"E6.24.3"),sQuery(id+"F0.wireOp",EDGE,"E6.25.0"),sQuery(id+"F0.wireOp",EDGE,"E6.25.1"),sQuery(id+"F0.wireOp",EDGE,"E6.25.2"),sQuery(id+"F0.wireOp",EDGE,"E6.25.3"),sQuery(id+"F0.wireOp",EDGE,"E6.26.0"),sQuery(id+"F0.wireOp",EDGE,"E6.26.1"),sQuery(id+"F0.wireOp",EDGE,"E6.26.2"),sQuery(id+"F0.wireOp",EDGE,"E6.26.3"),sQuery(id+"F0.wireOp",EDGE,"E6.27.0"),sQuery(id+"F0.wireOp",EDGE,"E6.27.1"),sQuery(id+"F0.wireOp",EDGE,"E6.27.2"),sQuery(id+"F0.wireOp",EDGE,"E6.27.3"),sQuery(id+"F0.wireOp",EDGE,"E6.28.0"),sQuery(id+"F0.wireOp",EDGE,"E6.28.1"),sQuery(id+"F0.wireOp",EDGE,"E6.28.2"),sQuery(id+"F0.wireOp",EDGE,"E6.28.3"),sQuery(id+"F0.wireOp",EDGE,"E6.29.0"),sQuery(id+"F0.wireOp",EDGE,"E6.29.1"),sQuery(id+"F0.wireOp",EDGE,"E6.29.2"),sQuery(id+"F0.wireOp",EDGE,"E6.29.3"),sQuery(id+"F0.wireOp",EDGE,"E6.30.0"),sQuery(id+"F0.wireOp",EDGE,"E6.30.1"),sQuery(id+"F0.wireOp",EDGE,"E6.30.2"),sQuery(id+"F0.wireOp",EDGE,"E6.30.3"),sQuery(id+"F0.wireOp",EDGE,"E6.31.0"),sQuery(id+"F0.wireOp",EDGE,"E6.31.1"),sQuery(id+"F0.wireOp",EDGE,"E6.31.2"),sQuery(id+"F0.wireOp",EDGE,"E6.31.3"),sQuery(id+"F0.wireOp",EDGE,"E6.32.0"),sQuery(id+"F0.wireOp",EDGE,"E6.32.1"),sQuery(id+"F0.wireOp",EDGE,"E6.32.2"),sQuery(id+"F0.wireOp",EDGE,"E6.32.3"),sQuery(id+"F0.wireOp",EDGE,"E6.33.0"),sQuery(id+"F0.wireOp",EDGE,"E6.33.1"),sQuery(id+"F0.wireOp",EDGE,"E6.33.2"),sQuery(id+"F0.wireOp",EDGE,"E6.33.3"),sQuery(id+"F0.wireOp",EDGE,"E6.34.0"),sQuery(id+"F0.wireOp",EDGE,"E6.34.1"),sQuery(id+"F0.wireOp",EDGE,"E6.34.2"),sQuery(id+"F0.wireOp",EDGE,"E6.34.3"),sQuery(id+"F0.wireOp",EDGE,"E6.35.0"),sQuery(id+"F0.wireOp",EDGE,"E6.35.1"),sQuery(id+"F0.wireOp",EDGE,"E6.35.2"),sQuery(id+"F0.wireOp",EDGE,"E6.35.3"),sQuery(id+"F0.wireOp",EDGE,"E6.36.0"),sQuery(id+"F0.wireOp",EDGE,"E6.36.1"),sQuery(id+"F0.wireOp",EDGE,"E6.36.2"),sQuery(id+"F0.wireOp",EDGE,"E6.36.3"),sQuery(id+"F0.wireOp",EDGE,"E6.37.0"),sQuery(id+"F0.wireOp",EDGE,"E6.37.1"),sQuery(id+"F0.wireOp",EDGE,"E6.37.2"),sQuery(id+"F0.wireOp",EDGE,"E6.37.3"),sQuery(id+"F0.wireOp",EDGE,"E6.38.0"),sQuery(id+"F0.wireOp",EDGE,"E6.38.1"),sQuery(id+"F0.wireOp",EDGE,"E6.38.2"),sQuery(id+"F0.wireOp",EDGE,"E6.38.3"),sQuery(id+"F0.wireOp",EDGE,"E6.39.0"),sQuery(id+"F0.wireOp",EDGE,"E6.39.1"),sQuery(id+"F0.wireOp",EDGE,"E6.39.2"),sQuery(id+"F0.wireOp",EDGE,"E6.39.3"),sQuery(id+"F0.wireOp",EDGE,"E6.40.0"),sQuery(id+"F0.wireOp",EDGE,"E6.40.1"),sQuery(id+"F0.wireOp",EDGE,"E6.40.2"),sQuery(id+"F0.wireOp",EDGE,"E6.40.3"),sQuery(id+"F0.wireOp",EDGE,"E6.41.0"),sQuery(id+"F0.wireOp",EDGE,"E6.41.1"),sQuery(id+"F0.wireOp",EDGE,"E6.41.2"),sQuery(id+"F0.wireOp",EDGE,"E6.41.3"),sQuery(id+"F0.wireOp",EDGE,"E6.42.0"),sQuery(id+"F0.wireOp",EDGE,"E6.42.1"),sQuery(id+"F0.wireOp",EDGE,"E6.42.2"),sQuery(id+"F0.wireOp",EDGE,"E6.42.3"),sQuery(id+"F0.wireOp",EDGE,"E6.43.0"),sQuery(id+"F0.wireOp",EDGE,"E6.43.1"),sQuery(id+"F0.wireOp",EDGE,"E6.43.2"),sQuery(id+"F0.wireOp",EDGE,"E6.43.3"),sQuery(id+"F0.wireOp",EDGE,"E6.44.0"),sQuery(id+"F0.wireOp",EDGE,"E6.44.1"),sQuery(id+"F0.wireOp",EDGE,"E6.44.2"),sQuery(id+"F0.wireOp",EDGE,"E6.44.3"),sQuery(id+"F0.wireOp",EDGE,"E6.45.0"),sQuery(id+"F0.wireOp",EDGE,"E6.45.1"),sQuery(id+"F0.wireOp",EDGE,"E6.45.2"),sQuery(id+"F0.wireOp",EDGE,"E6.45.3"),sQuery(id+"F0.wireOp",EDGE,"E6.46.0"),sQuery(id+"F0.wireOp",EDGE,"E6.46.1"),sQuery(id+"F0.wireOp",EDGE,"E6.46.2"),sQuery(id+"F0.wireOp",EDGE,"E6.46.3"),sQuery(id+"F0.wireOp",EDGE,"E6.47.0"),sQuery(id+"F0.wireOp",EDGE,"E6.47.1"),sQuery(id+"F0.wireOp",EDGE,"E6.47.2"),sQuery(id+"F0.wireOp",EDGE,"E6.47.3"),sQuery(id+"F0.wireOp",EDGE,"E6.48.0"),sQuery(id+"F0.wireOp",EDGE,"E6.48.1"),sQuery(id+"F0.wireOp",EDGE,"E6.48.2"),sQuery(id+"F0.wireOp",EDGE,"E6.48.3"),sQuery(id+"F0.wireOp",EDGE,"E6.49.0"),sQuery(id+"F0.wireOp",EDGE,"E6.49.1"),sQuery(id+"F0.wireOp",EDGE,"E6.49.2"),sQuery(id+"F0.wireOp",EDGE,"E6.49.3"),sQuery(id+"F0.wireOp",EDGE,"E6.50.0"),sQuery(id+"F0.wireOp",EDGE,"E6.50.1"),sQuery(id+"F0.wireOp",EDGE,"E6.50.2"),sQuery(id+"F0.wireOp",EDGE,"E6.50.3"),sQuery(id+"F0.wireOp",EDGE,"E6.51.0"),sQuery(id+"F0.wireOp",EDGE,"E6.51.1"),sQuery(id+"F0.wireOp",EDGE,"E6.51.2"),sQuery(id+"F0.wireOp",EDGE,"E6.51.3"),sQuery(id+"F0.wireOp",EDGE,"E6.52.0"),sQuery(id+"F0.wireOp",EDGE,"E6.52.1"),sQuery(id+"F0.wireOp",EDGE,"E6.52.2"),sQuery(id+"F0.wireOp",EDGE,"E6.52.3"),sQuery(id+"F0.wireOp",EDGE,"E6.53.0"),sQuery(id+"F0.wireOp",EDGE,"E6.53.1"),sQuery(id+"F0.wireOp",EDGE,"E6.53.2"),sQuery(id+"F0.wireOp",EDGE,"E6.53.3"),sQuery(id+"F0.wireOp",EDGE,"E6.54.0"),sQuery(id+"F0.wireOp",EDGE,"E6.54.1"),sQuery(id+"F0.wireOp",EDGE,"E6.54.2"),sQuery(id+"F0.wireOp",EDGE,"E6.54.3"),sQuery(id+"F0.wireOp",EDGE,"E6.55.0"),sQuery(id+"F0.wireOp",EDGE,"E6.55.1"),sQuery(id+"F0.wireOp",EDGE,"E6.55.2"),sQuery(id+"F0.wireOp",EDGE,"E6.55.3"),sQuery(id+"F0.wireOp",EDGE,"E6.56.0"),sQuery(id+"F0.wireOp",EDGE,"E6.56.1"),sQuery(id+"F0.wireOp",EDGE,"E6.56.2"),sQuery(id+"F0.wireOp",EDGE,"E6.56.3"),sQuery(id+"F0.wireOp",EDGE,"E6.57.0"),sQuery(id+"F0.wireOp",EDGE,"E6.57.1"),sQuery(id+"F0.wireOp",EDGE,"E6.57.2"),sQuery(id+"F0.wireOp",EDGE,"E6.57.3"),sQuery(id+"F0.wireOp",EDGE,"E6.58.0"),sQuery(id+"F0.wireOp",EDGE,"E6.58.1"),sQuery(id+"F0.wireOp",EDGE,"E6.58.2"),sQuery(id+"F0.wireOp",EDGE,"E6.58.3"),sQuery(id+"F0.wireOp",EDGE,"E6.59.0"),sQuery(id+"F0.wireOp",EDGE,"E6.59.1"),sQuery(id+"F0.wireOp",EDGE,"E6.59.2"),sQuery(id+"F0.wireOp",EDGE,"E6.59.3"),sQuery(id+"F0.wireOp",EDGE,"E6.60.0"),sQuery(id+"F0.wireOp",EDGE,"E6.60.1"),sQuery(id+"F0.wireOp",EDGE,"E6.60.2"),sQuery(id+"F0.wireOp",EDGE,"E6.60.3"),sQuery(id+"F0.wireOp",EDGE,"E6.61.0"),sQuery(id+"F0.wireOp",EDGE,"E6.61.1"),sQuery(id+"F0.wireOp",EDGE,"E6.61.2"),sQuery(id+"F0.wireOp",EDGE,"E6.61.3"),sQuery(id+"F0.wireOp",EDGE,"E6.62.0"),sQuery(id+"F0.wireOp",EDGE,"E6.62.1"),sQuery(id+"F0.wireOp",EDGE,"E6.62.2"),sQuery(id+"F0.wireOp",EDGE,"E6.62.3"),sQuery(id+"F0.wireOp",EDGE,"E6.63.0"),sQuery(id+"F0.wireOp",EDGE,"E6.63.1"),sQuery(id+"F0.wireOp",EDGE,"E6.63.2"),sQuery(id+"F0.wireOp",EDGE,"E6.63.3"),sQuery(id+"F0.wireOp",EDGE,"E6.64.0"),sQuery(id+"F0.wireOp",EDGE,"E6.64.1"),sQuery(id+"F0.wireOp",EDGE,"E6.64.2"),sQuery(id+"F0.wireOp",EDGE,"E6.64.3"),sQuery(id+"F0.wireOp",EDGE,"E6.65.0"),sQuery(id+"F0.wireOp",EDGE,"E6.65.1"),sQuery(id+"F0.wireOp",EDGE,"E6.65.2"),sQuery(id+"F0.wireOp",EDGE,"E6.65.3"),sQuery(id+"F0.wireOp",EDGE,"E6.66.0"),sQuery(id+"F0.wireOp",EDGE,"E6.66.1"),sQuery(id+"F0.wireOp",EDGE,"E6.66.2"),sQuery(id+"F0.wireOp",EDGE,"E6.66.3"),sQuery(id+"F0.wireOp",EDGE,"E6.67.0"),sQuery(id+"F0.wireOp",EDGE,"E6.67.1"),sQuery(id+"F0.wireOp",EDGE,"E6.67.2"),sQuery(id+"F0.wireOp",EDGE,"E6.67.3"),sQuery(id+"F0.wireOp",EDGE,"E6.68.0"),sQuery(id+"F0.wireOp",EDGE,"E6.68.1"),sQuery(id+"F0.wireOp",EDGE,"E6.68.2"),sQuery(id+"F0.wireOp",EDGE,"E6.68.3"),sQuery(id+"F0.wireOp",EDGE,"E6.69.0"),sQuery(id+"F0.wireOp",EDGE,"E6.69.1"),sQuery(id+"F0.wireOp",EDGE,"E6.69.2"),sQuery(id+"F0.wireOp",EDGE,"E6.69.3"),sQuery(id+"F0.wireOp",EDGE,"E6.70.0"),sQuery(id+"F0.wireOp",EDGE,"E6.70.1"),sQuery(id+"F0.wireOp",EDGE,"E6.70.2"),sQuery(id+"F0.wireOp",EDGE,"E6.70.3"),sQuery(id+"F0.wireOp",EDGE,"E6.71.0"),sQuery(id+"F0.wireOp",EDGE,"E6.71.1"),sQuery(id+"F0.wireOp",EDGE,"E6.71.2"),sQuery(id+"F0.wireOp",EDGE,"E6.71.3")])],"isStart":true});
            var sketch = newSketch(context, id + "F2", { "sketchPlane" : qUnion([Q0])});
            skCircle(sketch, "E7", {"center": v(0, 0) * mm, "radius": 5 * mm});
            skSolve(sketch);
        }
        {
            var Q0;
            Q0=qSketchRegion(id+"F2",true);
            extrude(context, id + "F3", {"entities" : qUnion([Q0]), "operationType" : NewBodyOperationType.ADD, "depth" : 4 * mm});
        }
        {
            var Q0;
            Q0=makeQuery(id+"F1.opExtrude","CAP_FACE",FACE,{"disambiguationData":[OSD([sQuery(id+"F0.wireOp",EDGE,"E0"),sQuery(id+"F0.wireOp",EDGE,"E2"),sQuery(id+"F0.wireOp",EDGE,"E3"),sQuery(id+"F0.wireOp",EDGE,"E4.0.MirrorCS"),sQuery(id+"F0.wireOp",EDGE,"E5.0.MirrorCS"),sQuery(id+"F0.wireOp",EDGE,"E6.1.0"),sQuery(id+"F0.wireOp",EDGE,"E6.1.1"),sQuery(id+"F0.wireOp",EDGE,"E6.1.2"),sQuery(id+"F0.wireOp",EDGE,"E6.1.3"),sQuery(id+"F0.wireOp",EDGE,"E6.2.0"),sQuery(id+"F0.wireOp",EDGE,"E6.2.1"),sQuery(id+"F0.wireOp",EDGE,"E6.2.2"),sQuery(id+"F0.wireOp",EDGE,"E6.2.3"),sQuery(id+"F0.wireOp",EDGE,"E6.3.0"),sQuery(id+"F0.wireOp",EDGE,"E6.3.1"),sQuery(id+"F0.wireOp",EDGE,"E6.3.2"),sQuery(id+"F0.wireOp",EDGE,"E6.3.3"),sQuery(id+"F0.wireOp",EDGE,"E6.4.0"),sQuery(id+"F0.wireOp",EDGE,"E6.4.1"),sQuery(id+"F0.wireOp",EDGE,"E6.4.2"),sQuery(id+"F0.wireOp",EDGE,"E6.4.3"),sQuery(id+"F0.wireOp",EDGE,"E6.5.0"),sQuery(id+"F0.wireOp",EDGE,"E6.5.1"),sQuery(id+"F0.wireOp",EDGE,"E6.5.2"),sQuery(id+"F0.wireOp",EDGE,"E6.5.3"),sQuery(id+"F0.wireOp",EDGE,"E6.6.0"),sQuery(id+"F0.wireOp",EDGE,"E6.6.1"),sQuery(id+"F0.wireOp",EDGE,"E6.6.2"),sQuery(id+"F0.wireOp",EDGE,"E6.6.3"),sQuery(id+"F0.wireOp",EDGE,"E6.7.0"),sQuery(id+"F0.wireOp",EDGE,"E6.7.1"),sQuery(id+"F0.wireOp",EDGE,"E6.7.2"),sQuery(id+"F0.wireOp",EDGE,"E6.7.3"),sQuery(id+"F0.wireOp",EDGE,"E6.8.0"),sQuery(id+"F0.wireOp",EDGE,"E6.8.1"),sQuery(id+"F0.wireOp",EDGE,"E6.8.2"),sQuery(id+"F0.wireOp",EDGE,"E6.8.3"),sQuery(id+"F0.wireOp",EDGE,"E6.9.0"),sQuery(id+"F0.wireOp",EDGE,"E6.9.1"),sQuery(id+"F0.wireOp",EDGE,"E6.9.2"),sQuery(id+"F0.wireOp",EDGE,"E6.9.3"),sQuery(id+"F0.wireOp",EDGE,"E6.10.0"),sQuery(id+"F0.wireOp",EDGE,"E6.10.1"),sQuery(id+"F0.wireOp",EDGE,"E6.10.2"),sQuery(id+"F0.wireOp",EDGE,"E6.10.3"),sQuery(id+"F0.wireOp",EDGE,"E6.11.0"),sQuery(id+"F0.wireOp",EDGE,"E6.11.1"),sQuery(id+"F0.wireOp",EDGE,"E6.11.2"),sQuery(id+"F0.wireOp",EDGE,"E6.11.3"),sQuery(id+"F0.wireOp",EDGE,"E6.12.0"),sQuery(id+"F0.wireOp",EDGE,"E6.12.1"),sQuery(id+"F0.wireOp",EDGE,"E6.12.2"),sQuery(id+"F0.wireOp",EDGE,"E6.12.3"),sQuery(id+"F0.wireOp",EDGE,"E6.13.0"),sQuery(id+"F0.wireOp",EDGE,"E6.13.1"),sQuery(id+"F0.wireOp",EDGE,"E6.13.2"),sQuery(id+"F0.wireOp",EDGE,"E6.13.3"),sQuery(id+"F0.wireOp",EDGE,"E6.14.0"),sQuery(id+"F0.wireOp",EDGE,"E6.14.1"),sQuery(id+"F0.wireOp",EDGE,"E6.14.2"),sQuery(id+"F0.wireOp",EDGE,"E6.14.3"),sQuery(id+"F0.wireOp",EDGE,"E6.15.0"),sQuery(id+"F0.wireOp",EDGE,"E6.15.1"),sQuery(id+"F0.wireOp",EDGE,"E6.15.2"),sQuery(id+"F0.wireOp",EDGE,"E6.15.3"),sQuery(id+"F0.wireOp",EDGE,"E6.16.0"),sQuery(id+"F0.wireOp",EDGE,"E6.16.1"),sQuery(id+"F0.wireOp",EDGE,"E6.16.2"),sQuery(id+"F0.wireOp",EDGE,"E6.16.3"),sQuery(id+"F0.wireOp",EDGE,"E6.17.0"),sQuery(id+"F0.wireOp",EDGE,"E6.17.1"),sQuery(id+"F0.wireOp",EDGE,"E6.17.2"),sQuery(id+"F0.wireOp",EDGE,"E6.17.3"),sQuery(id+"F0.wireOp",EDGE,"E6.18.0"),sQuery(id+"F0.wireOp",EDGE,"E6.18.1"),sQuery(id+"F0.wireOp",EDGE,"E6.18.2"),sQuery(id+"F0.wireOp",EDGE,"E6.18.3"),sQuery(id+"F0.wireOp",EDGE,"E6.19.0"),sQuery(id+"F0.wireOp",EDGE,"E6.19.1"),sQuery(id+"F0.wireOp",EDGE,"E6.19.2"),sQuery(id+"F0.wireOp",EDGE,"E6.19.3"),sQuery(id+"F0.wireOp",EDGE,"E6.20.0"),sQuery(id+"F0.wireOp",EDGE,"E6.20.1"),sQuery(id+"F0.wireOp",EDGE,"E6.20.2"),sQuery(id+"F0.wireOp",EDGE,"E6.20.3"),sQuery(id+"F0.wireOp",EDGE,"E6.21.0"),sQuery(id+"F0.wireOp",EDGE,"E6.21.1"),sQuery(id+"F0.wireOp",EDGE,"E6.21.2"),sQuery(id+"F0.wireOp",EDGE,"E6.21.3"),sQuery(id+"F0.wireOp",EDGE,"E6.22.0"),sQuery(id+"F0.wireOp",EDGE,"E6.22.1"),sQuery(id+"F0.wireOp",EDGE,"E6.22.2"),sQuery(id+"F0.wireOp",EDGE,"E6.22.3"),sQuery(id+"F0.wireOp",EDGE,"E6.23.0"),sQuery(id+"F0.wireOp",EDGE,"E6.23.1"),sQuery(id+"F0.wireOp",EDGE,"E6.23.2"),sQuery(id+"F0.wireOp",EDGE,"E6.23.3"),sQuery(id+"F0.wireOp",EDGE,"E6.24.0"),sQuery(id+"F0.wireOp",EDGE,"E6.24.1"),sQuery(id+"F0.wireOp",EDGE,"E6.24.2"),sQuery(id+"F0.wireOp",EDGE,"E6.24.3"),sQuery(id+"F0.wireOp",EDGE,"E6.25.0"),sQuery(id+"F0.wireOp",EDGE,"E6.25.1"),sQuery(id+"F0.wireOp",EDGE,"E6.25.2"),sQuery(id+"F0.wireOp",EDGE,"E6.25.3"),sQuery(id+"F0.wireOp",EDGE,"E6.26.0"),sQuery(id+"F0.wireOp",EDGE,"E6.26.1"),sQuery(id+"F0.wireOp",EDGE,"E6.26.2"),sQuery(id+"F0.wireOp",EDGE,"E6.26.3"),sQuery(id+"F0.wireOp",EDGE,"E6.27.0"),sQuery(id+"F0.wireOp",EDGE,"E6.27.1"),sQuery(id+"F0.wireOp",EDGE,"E6.27.2"),sQuery(id+"F0.wireOp",EDGE,"E6.27.3"),sQuery(id+"F0.wireOp",EDGE,"E6.28.0"),sQuery(id+"F0.wireOp",EDGE,"E6.28.1"),sQuery(id+"F0.wireOp",EDGE,"E6.28.2"),sQuery(id+"F0.wireOp",EDGE,"E6.28.3"),sQuery(id+"F0.wireOp",EDGE,"E6.29.0"),sQuery(id+"F0.wireOp",EDGE,"E6.29.1"),sQuery(id+"F0.wireOp",EDGE,"E6.29.2"),sQuery(id+"F0.wireOp",EDGE,"E6.29.3"),sQuery(id+"F0.wireOp",EDGE,"E6.30.0"),sQuery(id+"F0.wireOp",EDGE,"E6.30.1"),sQuery(id+"F0.wireOp",EDGE,"E6.30.2"),sQuery(id+"F0.wireOp",EDGE,"E6.30.3"),sQuery(id+"F0.wireOp",EDGE,"E6.31.0"),sQuery(id+"F0.wireOp",EDGE,"E6.31.1"),sQuery(id+"F0.wireOp",EDGE,"E6.31.2"),sQuery(id+"F0.wireOp",EDGE,"E6.31.3"),sQuery(id+"F0.wireOp",EDGE,"E6.32.0"),sQuery(id+"F0.wireOp",EDGE,"E6.32.1"),sQuery(id+"F0.wireOp",EDGE,"E6.32.2"),sQuery(id+"F0.wireOp",EDGE,"E6.32.3"),sQuery(id+"F0.wireOp",EDGE,"E6.33.0"),sQuery(id+"F0.wireOp",EDGE,"E6.33.1"),sQuery(id+"F0.wireOp",EDGE,"E6.33.2"),sQuery(id+"F0.wireOp",EDGE,"E6.33.3"),sQuery(id+"F0.wireOp",EDGE,"E6.34.0"),sQuery(id+"F0.wireOp",EDGE,"E6.34.1"),sQuery(id+"F0.wireOp",EDGE,"E6.34.2"),sQuery(id+"F0.wireOp",EDGE,"E6.34.3"),sQuery(id+"F0.wireOp",EDGE,"E6.35.0"),sQuery(id+"F0.wireOp",EDGE,"E6.35.1"),sQuery(id+"F0.wireOp",EDGE,"E6.35.2"),sQuery(id+"F0.wireOp",EDGE,"E6.35.3"),sQuery(id+"F0.wireOp",EDGE,"E6.36.0"),sQuery(id+"F0.wireOp",EDGE,"E6.36.1"),sQuery(id+"F0.wireOp",EDGE,"E6.36.2"),sQuery(id+"F0.wireOp",EDGE,"E6.36.3"),sQuery(id+"F0.wireOp",EDGE,"E6.37.0"),sQuery(id+"F0.wireOp",EDGE,"E6.37.1"),sQuery(id+"F0.wireOp",EDGE,"E6.37.2"),sQuery(id+"F0.wireOp",EDGE,"E6.37.3"),sQuery(id+"F0.wireOp",EDGE,"E6.38.0"),sQuery(id+"F0.wireOp",EDGE,"E6.38.1"),sQuery(id+"F0.wireOp",EDGE,"E6.38.2"),sQuery(id+"F0.wireOp",EDGE,"E6.38.3"),sQuery(id+"F0.wireOp",EDGE,"E6.39.0"),sQuery(id+"F0.wireOp",EDGE,"E6.39.1"),sQuery(id+"F0.wireOp",EDGE,"E6.39.2"),sQuery(id+"F0.wireOp",EDGE,"E6.39.3"),sQuery(id+"F0.wireOp",EDGE,"E6.40.0"),sQuery(id+"F0.wireOp",EDGE,"E6.40.1"),sQuery(id+"F0.wireOp",EDGE,"E6.40.2"),sQuery(id+"F0.wireOp",EDGE,"E6.40.3"),sQuery(id+"F0.wireOp",EDGE,"E6.41.0"),sQuery(id+"F0.wireOp",EDGE,"E6.41.1"),sQuery(id+"F0.wireOp",EDGE,"E6.41.2"),sQuery(id+"F0.wireOp",EDGE,"E6.41.3"),sQuery(id+"F0.wireOp",EDGE,"E6.42.0"),sQuery(id+"F0.wireOp",EDGE,"E6.42.1"),sQuery(id+"F0.wireOp",EDGE,"E6.42.2"),sQuery(id+"F0.wireOp",EDGE,"E6.42.3"),sQuery(id+"F0.wireOp",EDGE,"E6.43.0"),sQuery(id+"F0.wireOp",EDGE,"E6.43.1"),sQuery(id+"F0.wireOp",EDGE,"E6.43.2"),sQuery(id+"F0.wireOp",EDGE,"E6.43.3"),sQuery(id+"F0.wireOp",EDGE,"E6.44.0"),sQuery(id+"F0.wireOp",EDGE,"E6.44.1"),sQuery(id+"F0.wireOp",EDGE,"E6.44.2"),sQuery(id+"F0.wireOp",EDGE,"E6.44.3"),sQuery(id+"F0.wireOp",EDGE,"E6.45.0"),sQuery(id+"F0.wireOp",EDGE,"E6.45.1"),sQuery(id+"F0.wireOp",EDGE,"E6.45.2"),sQuery(id+"F0.wireOp",EDGE,"E6.45.3"),sQuery(id+"F0.wireOp",EDGE,"E6.46.0"),sQuery(id+"F0.wireOp",EDGE,"E6.46.1"),sQuery(id+"F0.wireOp",EDGE,"E6.46.2"),sQuery(id+"F0.wireOp",EDGE,"E6.46.3"),sQuery(id+"F0.wireOp",EDGE,"E6.47.0"),sQuery(id+"F0.wireOp",EDGE,"E6.47.1"),sQuery(id+"F0.wireOp",EDGE,"E6.47.2"),sQuery(id+"F0.wireOp",EDGE,"E6.47.3"),sQuery(id+"F0.wireOp",EDGE,"E6.48.0"),sQuery(id+"F0.wireOp",EDGE,"E6.48.1"),sQuery(id+"F0.wireOp",EDGE,"E6.48.2"),sQuery(id+"F0.wireOp",EDGE,"E6.48.3"),sQuery(id+"F0.wireOp",EDGE,"E6.49.0"),sQuery(id+"F0.wireOp",EDGE,"E6.49.1"),sQuery(id+"F0.wireOp",EDGE,"E6.49.2"),sQuery(id+"F0.wireOp",EDGE,"E6.49.3"),sQuery(id+"F0.wireOp",EDGE,"E6.50.0"),sQuery(id+"F0.wireOp",EDGE,"E6.50.1"),sQuery(id+"F0.wireOp",EDGE,"E6.50.2"),sQuery(id+"F0.wireOp",EDGE,"E6.50.3"),sQuery(id+"F0.wireOp",EDGE,"E6.51.0"),sQuery(id+"F0.wireOp",EDGE,"E6.51.1"),sQuery(id+"F0.wireOp",EDGE,"E6.51.2"),sQuery(id+"F0.wireOp",EDGE,"E6.51.3"),sQuery(id+"F0.wireOp",EDGE,"E6.52.0"),sQuery(id+"F0.wireOp",EDGE,"E6.52.1"),sQuery(id+"F0.wireOp",EDGE,"E6.52.2"),sQuery(id+"F0.wireOp",EDGE,"E6.52.3"),sQuery(id+"F0.wireOp",EDGE,"E6.53.0"),sQuery(id+"F0.wireOp",EDGE,"E6.53.1"),sQuery(id+"F0.wireOp",EDGE,"E6.53.2"),sQuery(id+"F0.wireOp",EDGE,"E6.53.3"),sQuery(id+"F0.wireOp",EDGE,"E6.54.0"),sQuery(id+"F0.wireOp",EDGE,"E6.54.1"),sQuery(id+"F0.wireOp",EDGE,"E6.54.2"),sQuery(id+"F0.wireOp",EDGE,"E6.54.3"),sQuery(id+"F0.wireOp",EDGE,"E6.55.0"),sQuery(id+"F0.wireOp",EDGE,"E6.55.1"),sQuery(id+"F0.wireOp",EDGE,"E6.55.2"),sQuery(id+"F0.wireOp",EDGE,"E6.55.3"),sQuery(id+"F0.wireOp",EDGE,"E6.56.0"),sQuery(id+"F0.wireOp",EDGE,"E6.56.1"),sQuery(id+"F0.wireOp",EDGE,"E6.56.2"),sQuery(id+"F0.wireOp",EDGE,"E6.56.3"),sQuery(id+"F0.wireOp",EDGE,"E6.57.0"),sQuery(id+"F0.wireOp",EDGE,"E6.57.1"),sQuery(id+"F0.wireOp",EDGE,"E6.57.2"),sQuery(id+"F0.wireOp",EDGE,"E6.57.3"),sQuery(id+"F0.wireOp",EDGE,"E6.58.0"),sQuery(id+"F0.wireOp",EDGE,"E6.58.1"),sQuery(id+"F0.wireOp",EDGE,"E6.58.2"),sQuery(id+"F0.wireOp",EDGE,"E6.58.3"),sQuery(id+"F0.wireOp",EDGE,"E6.59.0"),sQuery(id+"F0.wireOp",EDGE,"E6.59.1"),sQuery(id+"F0.wireOp",EDGE,"E6.59.2"),sQuery(id+"F0.wireOp",EDGE,"E6.59.3"),sQuery(id+"F0.wireOp",EDGE,"E6.60.0"),sQuery(id+"F0.wireOp",EDGE,"E6.60.1"),sQuery(id+"F0.wireOp",EDGE,"E6.60.2"),sQuery(id+"F0.wireOp",EDGE,"E6.60.3"),sQuery(id+"F0.wireOp",EDGE,"E6.61.0"),sQuery(id+"F0.wireOp",EDGE,"E6.61.1"),sQuery(id+"F0.wireOp",EDGE,"E6.61.2"),sQuery(id+"F0.wireOp",EDGE,"E6.61.3"),sQuery(id+"F0.wireOp",EDGE,"E6.62.0"),sQuery(id+"F0.wireOp",EDGE,"E6.62.1"),sQuery(id+"F0.wireOp",EDGE,"E6.62.2"),sQuery(id+"F0.wireOp",EDGE,"E6.62.3"),sQuery(id+"F0.wireOp",EDGE,"E6.63.0"),sQuery(id+"F0.wireOp",EDGE,"E6.63.1"),sQuery(id+"F0.wireOp",EDGE,"E6.63.2"),sQuery(id+"F0.wireOp",EDGE,"E6.63.3"),sQuery(id+"F0.wireOp",EDGE,"E6.64.0"),sQuery(id+"F0.wireOp",EDGE,"E6.64.1"),sQuery(id+"F0.wireOp",EDGE,"E6.64.2"),sQuery(id+"F0.wireOp",EDGE,"E6.64.3"),sQuery(id+"F0.wireOp",EDGE,"E6.65.0"),sQuery(id+"F0.wireOp",EDGE,"E6.65.1"),sQuery(id+"F0.wireOp",EDGE,"E6.65.2"),sQuery(id+"F0.wireOp",EDGE,"E6.65.3"),sQuery(id+"F0.wireOp",EDGE,"E6.66.0"),sQuery(id+"F0.wireOp",EDGE,"E6.66.1"),sQuery(id+"F0.wireOp",EDGE,"E6.66.2"),sQuery(id+"F0.wireOp",EDGE,"E6.66.3"),sQuery(id+"F0.wireOp",EDGE,"E6.67.0"),sQuery(id+"F0.wireOp",EDGE,"E6.67.1"),sQuery(id+"F0.wireOp",EDGE,"E6.67.2"),sQuery(id+"F0.wireOp",EDGE,"E6.67.3"),sQuery(id+"F0.wireOp",EDGE,"E6.68.0"),sQuery(id+"F0.wireOp",EDGE,"E6.68.1"),sQuery(id+"F0.wireOp",EDGE,"E6.68.2"),sQuery(id+"F0.wireOp",EDGE,"E6.68.3"),sQuery(id+"F0.wireOp",EDGE,"E6.69.0"),sQuery(id+"F0.wireOp",EDGE,"E6.69.1"),sQuery(id+"F0.wireOp",EDGE,"E6.69.2"),sQuery(id+"F0.wireOp",EDGE,"E6.69.3"),sQuery(id+"F0.wireOp",EDGE,"E6.70.0"),sQuery(id+"F0.wireOp",EDGE,"E6.70.1"),sQuery(id+"F0.wireOp",EDGE,"E6.70.2"),sQuery(id+"F0.wireOp",EDGE,"E6.70.3"),sQuery(id+"F0.wireOp",EDGE,"E6.71.0"),sQuery(id+"F0.wireOp",EDGE,"E6.71.1"),sQuery(id+"F0.wireOp",EDGE,"E6.71.2"),sQuery(id+"F0.wireOp",EDGE,"E6.71.3")])],"isStart":false});
            var sketch = newSketch(context, id + "F4", { "sketchPlane" : qUnion([Q0])});
            skCircle(sketch, "E8", {"center": v(0, 0) * mm, "radius": 0.75 * mm});
            skSolve(sketch);
        }
        {
            var Q0;
            Q0=qSketchRegion(id+"F4",true);
            extrude(context, id + "F5", {"entities" : qUnion([Q0]), "operationType" : NewBodyOperationType.REMOVE, "oppositeDirection" : true, "depth" : 25 * mm});
        }
    });
